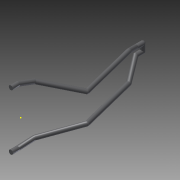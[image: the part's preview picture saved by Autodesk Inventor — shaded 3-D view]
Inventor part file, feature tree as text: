
AUTODESK INVENTOR PART (.ipt)
format: ipt  version: 2013 (Build 170138000, 138)  size: 160,256 bytes
history: native  units: mm
features: sketch x12, plane x8, other x1, sweep x1, mirror x1, fillet x1
ambient origin geometry x8: Origin, YZ Plane, XZ Plane, XY Plane, X Axis, Y Axis, Z Axis, Center Point
feature tree (24):
  other  "Sólido2"
  sketch  "Boceto1"  dims[d0=16.5mm d1=3.5mm d2=0.4mm]
  sketch  "Boceto2"  dims[d8=-0.5mm]
  plane  "Plano de trabajo1"
  sketch  "Boceto3"  dims[d11=3.5mm]
  plane  "Plano de trabajo2"
  sketch  "Boceto4"  dims[d15=1.0mm]
  plane  "Plano de trabajo3"
  sketch  "Boceto5"  dims[d16=-2.0mm]
  plane  "Plano de trabajo4"
  sketch  "Boceto6"  dims[d19=1.0mm]
  sketch  "Boceto 3D1"  dims[d3=-0.4mm]
  sketch  "Boceto7"  dims[d21=1.0mm]
  plane  "Plano de trabajo5"
  sketch  "Boceto8"  dims[d22=-3.5mm]
  plane  "Plano de trabajo6"
  sketch  "Boceto9"  dims[d23=16.5mm]
  plane  "Plano de trabajo7"
  sketch  "Boceto10"  dims[d24=1.0mm]
  plane  "Plano de trabajo8"
  sketch  "Boceto11"  dims[d25=-1.0mm d27=0.6mm d28=18.5mm d34=-4.0mm d37=0.5mm d39=8.0mm d40=0.0mm d41=0.3mm]
  sweep  "Barrido3"
  mirror  "Simetría3"
  fillet  "Empalme2"  Radius=0.4mm
